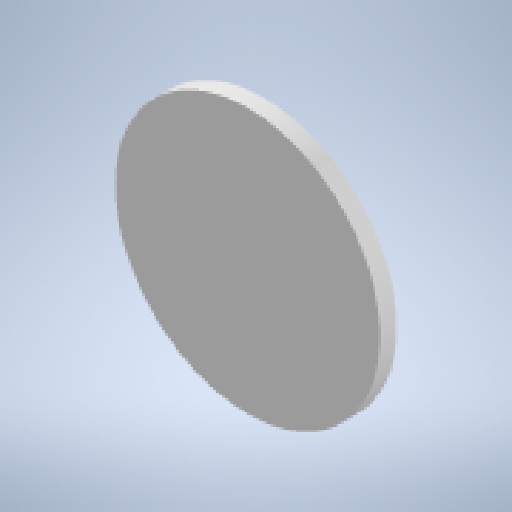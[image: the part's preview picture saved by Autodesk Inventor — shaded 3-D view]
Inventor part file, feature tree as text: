
AUTODESK INVENTOR PART (.ipt)
format: ipt  version: 2023 (Build 270158000, 158)  size: 126,976 bytes
history: native  units: mm
features: other x3, reference x2, extrude x1, sketch x1
ambient origin geometry x8: Origin, YZ Plane, XZ Plane, XY Plane, X Axis, Y Axis, Z Axis, Center Point
bodies: Solid1 (feature_tree)
feature tree (7):
  extrude  "Extrusion1"  Depth=5.0mm
  sketch  "Sketch1"  dims[d0=9.5mm d1=80.0mm d2=5.0mm d3=0.0mm d4=0.5mm d5=0.872665mm d6=0.5mm d7=0.872665mm]
  reference  "Reference1"
  reference  "Reference2"
  other  "<userpath>\OneDrive\Namizje\school\4. letnik\Matura\Izdelovanje\3D model\3D_skenner.iam"
  other  "3D_skenner.iam"
  other  "Ogrodje_spodaj_1:1"
